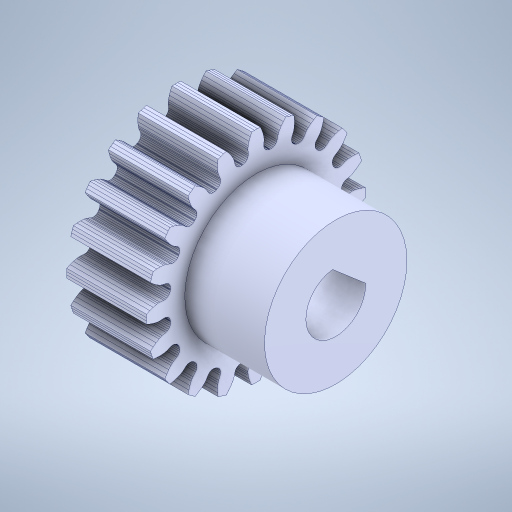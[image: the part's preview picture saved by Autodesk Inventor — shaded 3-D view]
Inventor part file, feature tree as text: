
AUTODESK INVENTOR PART (.ipt)
format: ipt  version: 2023.5 (Build 275446000, 446)  size: 801,280 bytes
history: native  units: mm
features: extrude x2, other x2, sketch x2
ambient origin geometry x8: Origin, YZ Plane, XZ Plane, XY Plane, X Axis, Y Axis, Z Axis, Center Point
bodies: Body1 (feature_tree)
feature tree (6):
  extrude  "Wyciągnięcie proste1"  Depth=2.0mm
  extrude  "Wyciągnięcie proste2"  Depth=4.0mm TaperAngle=0.0deg
  other  "Bryła31"
  sketch  "Szkic1"
  sketch  "Szkic2"
  other  "Engrane_8:1"
